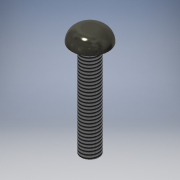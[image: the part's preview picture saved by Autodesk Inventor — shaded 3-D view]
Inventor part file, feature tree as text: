
AUTODESK INVENTOR PART (.ipt)
format: ipt  version: 2020.2 (Build 242310000, 310)  size: 142,336 bytes
history: native  units: mm
features: extrude x4, sketch x4, other x1, fillet x1, thread x1
ambient origin geometry x1: Origin
bodies: Body1 (feature_tree)
feature tree (11):
  other  "ソリッド1"
  extrude  "押し出し1"  Depth=3.0mm
  extrude  "押し出し2"  Depth=6.0mm TaperAngle=0.0deg
  fillet  "フィレット1"  Radius=6.0mm
  thread  "ねじ1"
  extrude  "押し出し3"  Depth=2.0mm TaperAngle=0.0deg
  extrude  "押し出し4"  Depth=2.0mm
  sketch  "スケッチ1"
  sketch  "スケッチ2"
  sketch  "スケッチ3"
  sketch  "スケッチ4"
